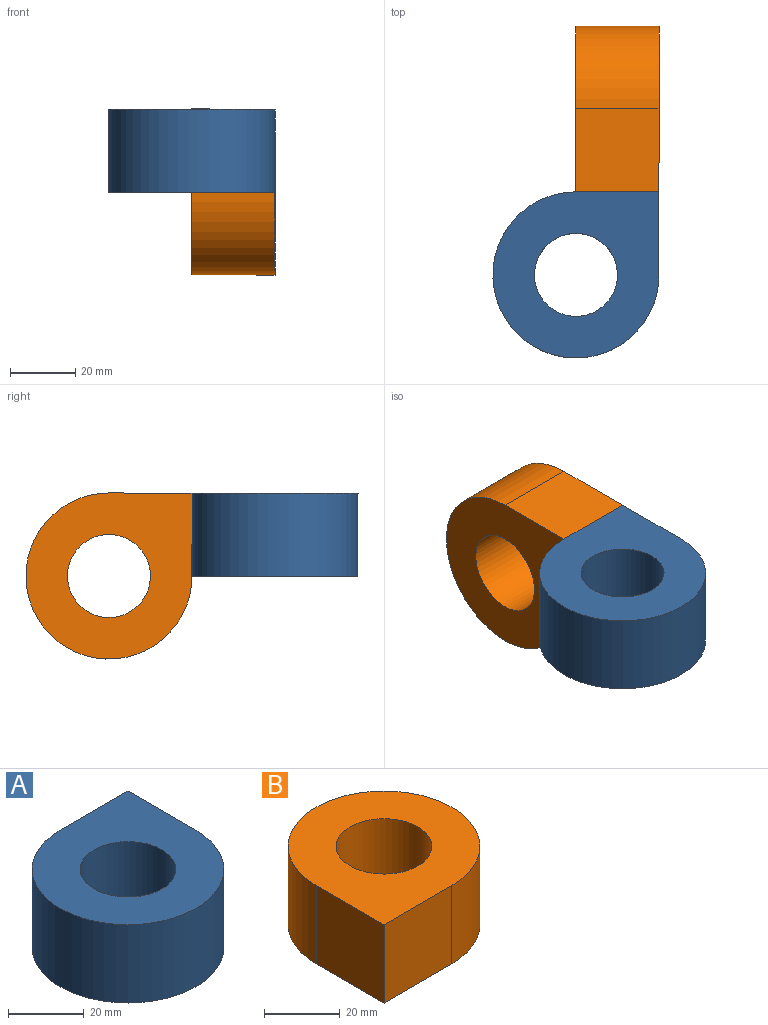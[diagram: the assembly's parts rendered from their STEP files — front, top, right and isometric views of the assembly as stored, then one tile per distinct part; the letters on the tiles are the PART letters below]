
ASSEMBLY  parts=2 mates=1
PART A: 6 faces, bbox 50.8x50.8x25.4 mm
  f0: plane 25.4x25.4mm, normal (0,1,0), area 645.2mm2, adj f1,f2,f3,f4
  f1: plane 25.4x25.4mm, normal (1,0,0), area 645.2mm2, adj f0,f2,f3,f4
  f2: plane 50.8x50.8mm, normal (0,0,1), area 1658.6mm2, adj f0,f1,f4,f5
  f3: plane 50.8x50.8mm, normal (0,0,-1), area 1658.6mm2, adj f0,f1,f4,f5
  f4: cylinder r=25.4mm len=50.8mm, axis (0,0,-1), area 3040.2mm2, adj f0,f1,f2,f3
  f5: cylinder r=12.7mm len=25.4mm, axis (0,0,1), area 2026.8mm2, adj f2,f3
PART B: 6 faces, bbox 50.8x50.8x25.4 mm
  f0: plane 25.4x25.4mm, normal (0,-1,0), area 645.2mm2, adj f1,f2,f3,f4
  f1: plane 25.4x25.4mm, normal (-1,0,0), area 645.2mm2, adj f0,f2,f3,f4
  f2: plane 50.8x50.8mm, normal (0,0,1), area 1658.6mm2, adj f0,f1,f4,f5
  f3: plane 50.8x50.8mm, normal (0,0,-1), area 1658.6mm2, adj f0,f1,f4,f5
  f4: cylinder r=25.4mm len=50.8mm, axis (0,0,1), area 3040.2mm2, adj f0,f1,f2,f3
  f5: cylinder r=12.7mm len=25.4mm, axis (0,0,1), area 2026.8mm2, adj f2,f3
PLACE A rot(axis=(-0.71,-0.71,0),180deg) t=(15.2,50.31,-14.37)mm
PLACE B rot(axis=(0,1,0),90deg) t=(15.2,101.11,11.03)mm
MATE parallel B.f0 <-> A.f1  axis (0,-1,0) through (27.9,75.71,-27.07)mm
